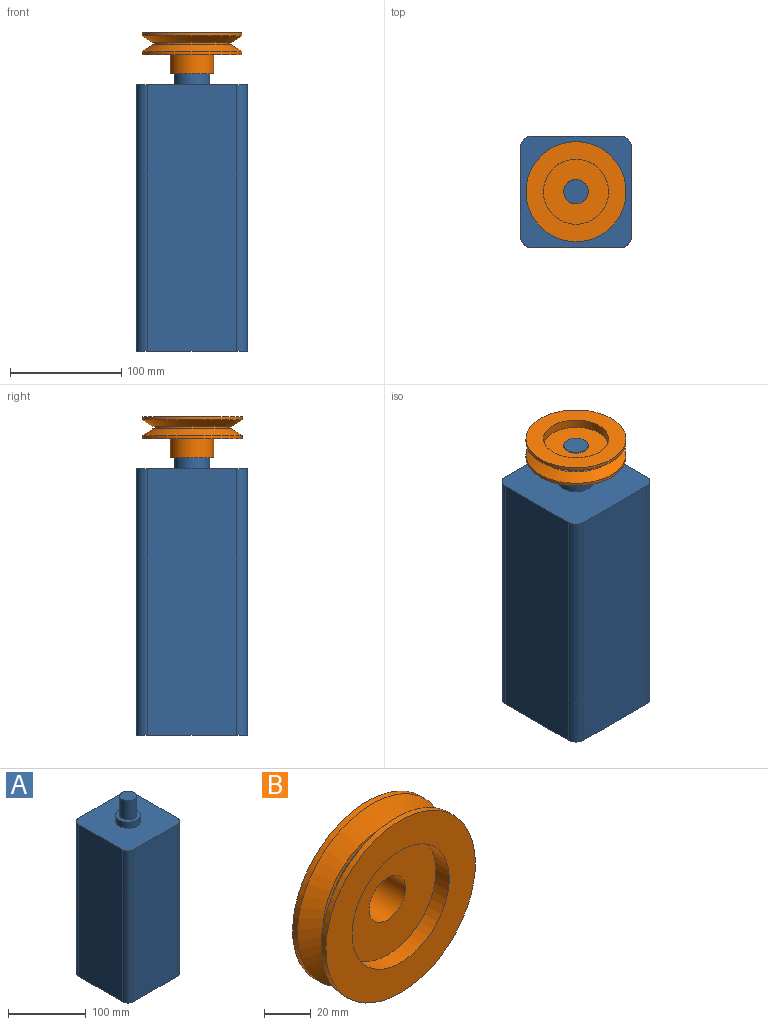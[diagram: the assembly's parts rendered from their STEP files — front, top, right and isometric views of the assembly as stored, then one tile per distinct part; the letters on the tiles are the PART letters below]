
ASSEMBLY  parts=2 mates=1
PART A: 14 faces, bbox 100x100x280 mm
  f0: plane 240x80mm, normal (1,0,0), area 19200mm2, adj f1,f7,f8,f9
  f1: cylinder r=10mm len=240mm, axis (0,0,-1), area 3769.9mm2, adj f0,f2,f8,f9
  f2: plane 240x80mm, normal (0,1,0), area 19200mm2, adj f1,f3,f8,f9
  f3: cylinder r=10mm len=240mm, axis (0,0,-1), area 3769.9mm2, adj f2,f4,f8,f9
  f4: plane 240x80mm, normal (-1,0,0), area 19200mm2, adj f3,f5,f8,f9
  f5: cylinder r=10mm len=240mm, axis (0,0,-1), area 3769.9mm2, adj f4,f6,f8,f9
  f6: plane 240x80mm, normal (0,-1,0), area 19200mm2, adj f5,f7,f8,f9
  f7: cylinder r=10mm len=240mm, axis (0,0,-1), area 3769.9mm2, adj f0,f6,f8,f9
  f8: plane 100x100mm, normal (0,0,1), area 9109.9mm2, adj f0,f1,f2,f3,f4,f5,f6,f7
  f9: plane 100x100mm, normal (0,0,-1), area 9914.2mm2, adj f0,f1,f2,f3,f4,f5,f6,f7
  f10: cylinder r=16mm len=32mm, axis (0,0,-1), area 1005.3mm2, adj f8,f11
  f11: plane 32x32mm, normal (0,0,1), area 424.1mm2, adj f10,f12
  f12: cylinder r=11mm len=30mm, axis (0,0,-1), area 2073.5mm2, adj f11,f13
  f13: plane 22x22mm, normal (0,0,1), area 380.1mm2, adj f12
PART B: 14 faces, bbox 90x37x90 mm
  f0: cylinder r=19.66mm len=39.32mm, axis (0,-1,0), area 2100.2mm2, adj f1,f13
  f1: plane 90x90mm, normal (0,1,0), area 5147.2mm2, adj f0,f2
  f2: cylinder r=45mm len=90mm, axis (0,-1,0), area 802.1mm2, adj f1,f3
  f3: cone r=35.57mm half-angle=57.7deg, axis (0,1,0), area 2823.5mm2, adj f2,f4
  f4: plane 71.14x71.14mm, normal (0,-1,0), area 401.5mm2, adj f3,f5
  f5: cylinder r=33.73mm len=67.45mm, axis (0,-1,0), area 481mm2, adj f4,f6
  f6: plane 71.42x71.42mm, normal (0,1,0), area 433.3mm2, adj f5,f7
  f7: cone r=45mm half-angle=56.7deg, axis (0,-1,0), area 2817.7mm2, adj f6,f8
  f8: cylinder r=45mm len=90mm, axis (0,-1,0), area 801.4mm2, adj f7,f9
  f9: plane 90x90mm, normal (0,-1,0), area 3666mm2, adj f8,f10
  f10: cylinder r=29.29mm len=58.59mm, axis (0,-1,0), area 1472.4mm2, adj f9,f11
  f11: plane 58.59x58.59mm, normal (0,-1,0), area 2315.6mm2, adj f10,f12
  f12: cylinder r=11mm len=29mm, axis (0,-1,0), area 2004.3mm2, adj f11,f13
  f13: plane 39.32x39.32mm, normal (0,1,0), area 834.4mm2, adj f0,f12
PLACE A t=(-29.35,46.55,-44.76)mm
PLACE B rot(axis=(-1,0,0),90deg) t=(-29.35,46.55,242.24)mm
MATE fastened B.f0 <-> A.f10  axis (0,0,-1) through (-29.35,46.55,205.24)mm
